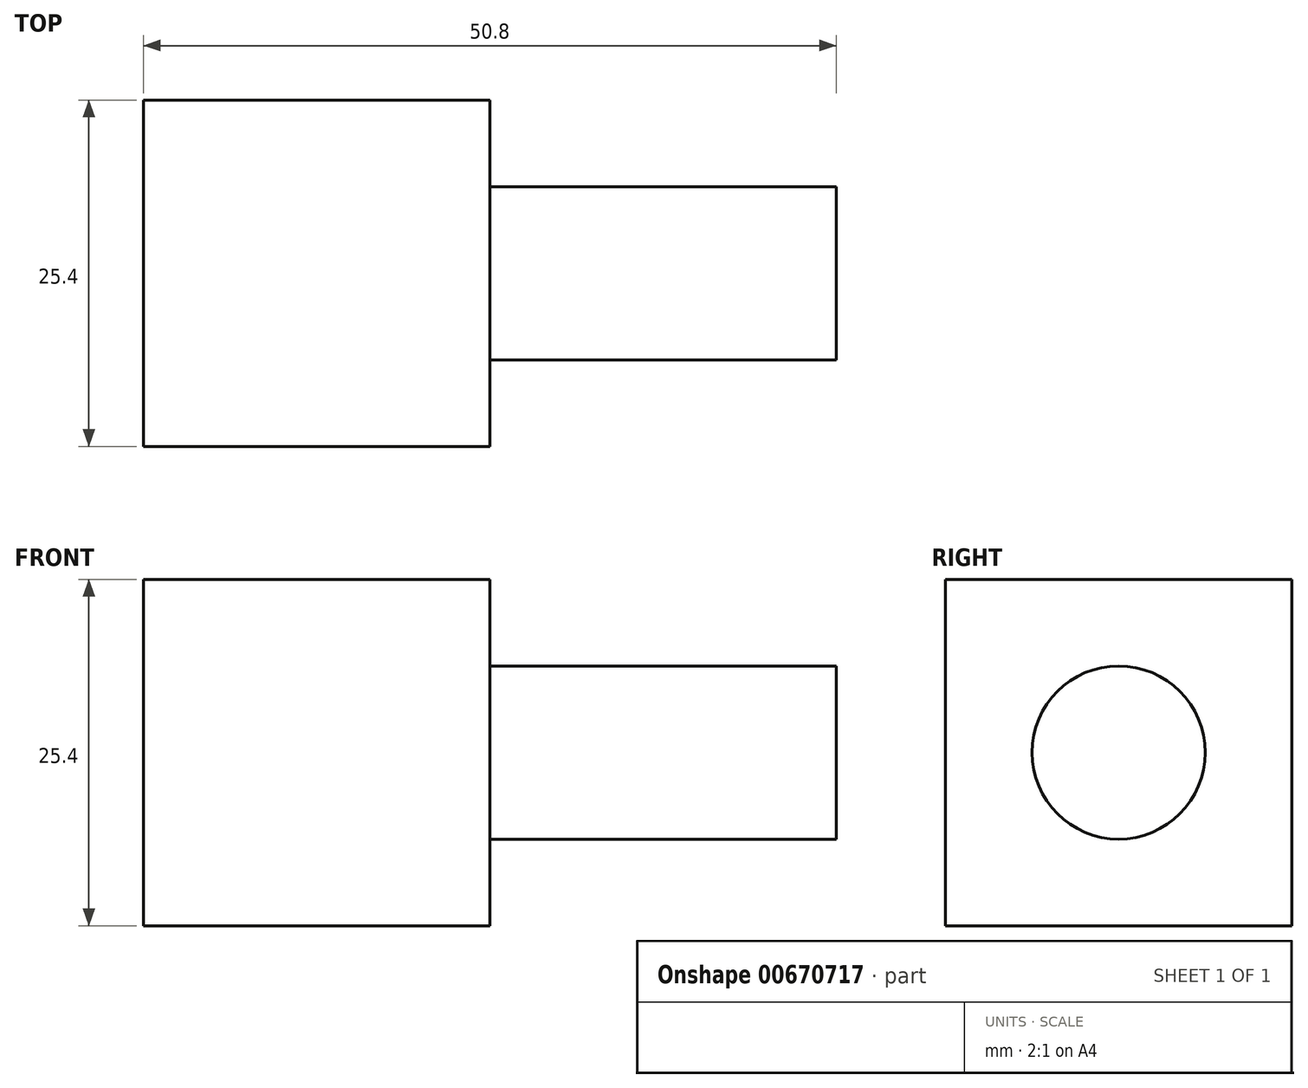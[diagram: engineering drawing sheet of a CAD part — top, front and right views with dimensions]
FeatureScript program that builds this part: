
annotation { "Feature Type Name" : "Feature", "Feature Type Description" : "" }
export const myFeature = defineFeature(function(context is Context, id is Id, definition is map)
    precondition{}
    {
        {
            var Q0;
            Q0=qCreatedBy(makeId("Top.planeOp"),FACE);
            var sketch = newSketch(context, id + "F0", { "sketchPlane" : qUnion([Q0])});
            skLineSegment(sketch, "E0.bottom", {"start": v(-12.7, 12.7) * mm, "end": v(12.7, 12.7) * mm});
            skLineSegment(sketch, "E0.top", {"start": v(-12.7, -12.7) * mm, "end": v(12.7, -12.7) * mm});
            skLineSegment(sketch, "E0.left", {"start": v(-12.7, 12.7) * mm, "end": v(-12.7, -12.7) * mm});
            skLineSegment(sketch, "E0.right", {"start": v(12.7, 12.7) * mm, "end": v(12.7, -12.7) * mm});
            skPoint(sketch, "E0.middle", {"position": v(0, 0) * mm});
            skSolve(sketch);
        }
        {
            var Q0;
            Q0=makeQuery(id+"F0.imprint","IMPRINT",FACE,{"disambiguationData":[TD([[makeQuery(id+"F0.imprint","IMPRINT",EDGE,{"derivedFrom":sQuery(id+"F0.wireOp",EDGE,"E0.bottom")}),-1.0]])]});
            extrude(context, id + "F1", {"entities" : qUnion([Q0]), "depth" : 25.4 * mm, "offsetDistance" : 25.4 * mm});
        }
        {
            var Q0;
            Q0=makeQuery(id+"F1.opExtrude","SWEPT_FACE",FACE,{"disambiguationData":[OSD([sQuery(id+"F0.wireOp",EDGE,"E0.right")])]});
            var sketch = newSketch(context, id + "F2", { "sketchPlane" : qUnion([Q0])});
            skCircle(sketch, "E1", {"center": v(0, 12.7) * mm, "radius": 6.35 * mm});
            skSolve(sketch);
        }
        {
            var Q0;
            Q0=makeQuery(id+"F2.imprint","IMPRINT",FACE,{"disambiguationData":[TD([[makeQuery(id+"F2.imprint","IMPRINT",EDGE,{"derivedFrom":sQuery(id+"F2.wireOp",EDGE,"E1")}),1.0]])]});
            extrude(context, id + "F3", {"entities" : qUnion([Q0]), "operationType" : NewBodyOperationType.ADD, "depth" : 25.4 * mm, "offsetDistance" : 25.4 * mm});
        }
    });
